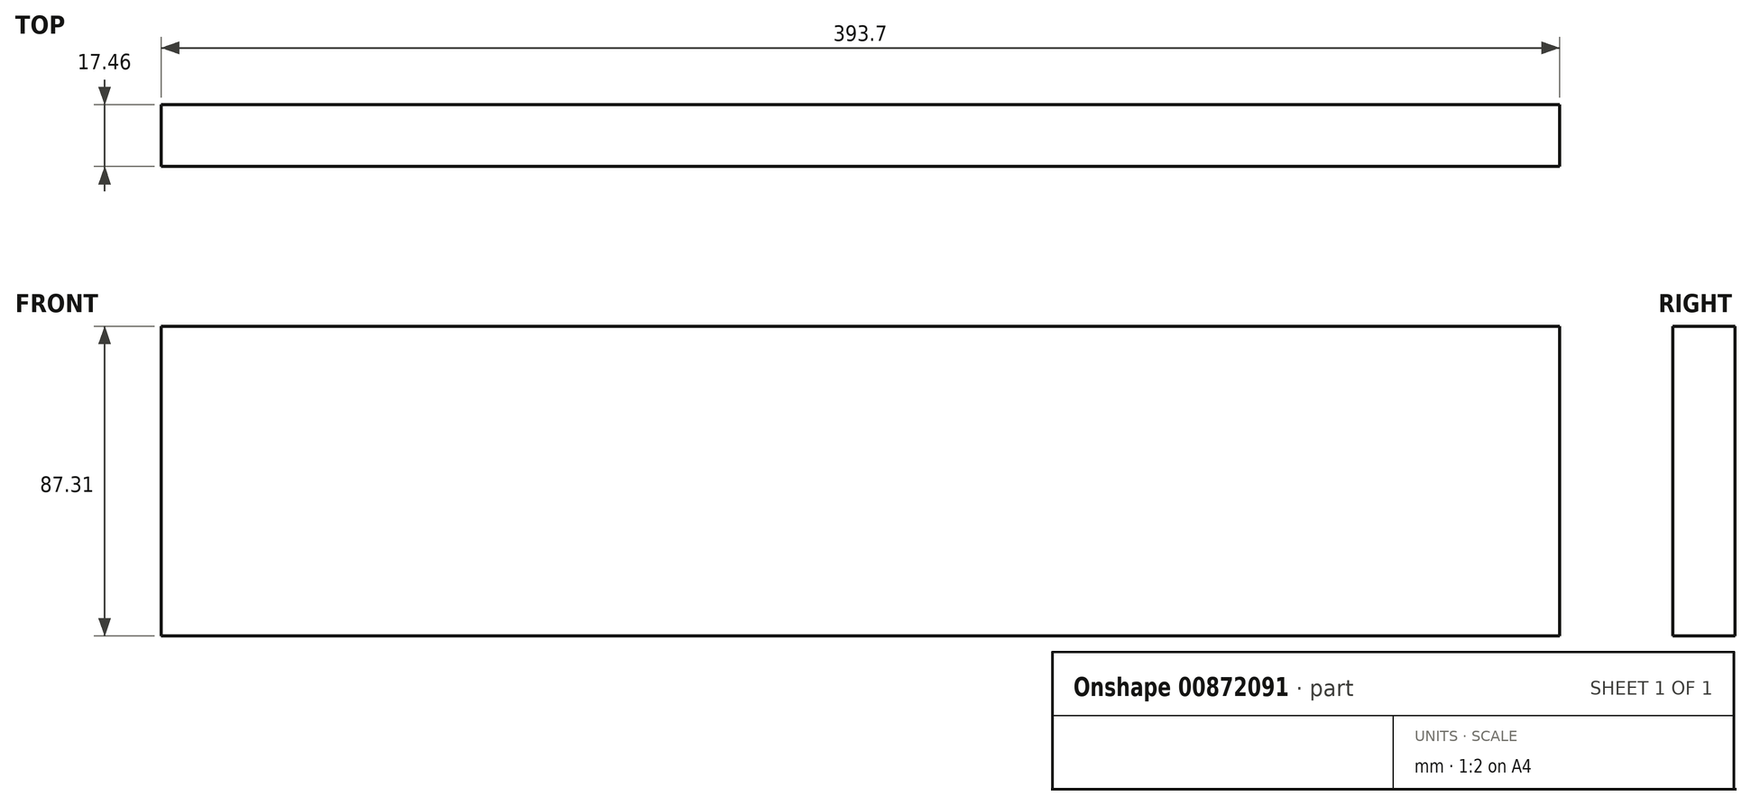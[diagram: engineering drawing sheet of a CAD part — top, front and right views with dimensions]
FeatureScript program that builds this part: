
annotation { "Feature Type Name" : "Feature", "Feature Type Description" : "" }
export const myFeature = defineFeature(function(context is Context, id is Id, definition is map)
    precondition{}
    {
        {
            var Q0;
            Q0=qCreatedBy(makeId("Front.planeOp"),FACE);
            var sketch = newSketch(context, id + "F0", { "sketchPlane" : qUnion([Q0])});
            skLineSegment(sketch, "E0.bottom", {"start": v(0, 0) * mm, "end": v(393.7, 0) * mm});
            skLineSegment(sketch, "E0.top", {"start": v(0, 87.31) * mm, "end": v(393.7, 87.31) * mm});
            skLineSegment(sketch, "E0.left", {"start": v(0, 0) * mm, "end": v(0, 87.31) * mm});
            skLineSegment(sketch, "E0.right", {"start": v(393.7, 0) * mm, "end": v(393.7, 87.31) * mm});
            skSolve(sketch);
        }
        {
            var Q0;
            Q0=qSketchRegion(id+"F0",true);
            extrude(context, id + "F1", {"entities" : qUnion([Q0]), "depth" : 17.46 * mm});
        }
    });
